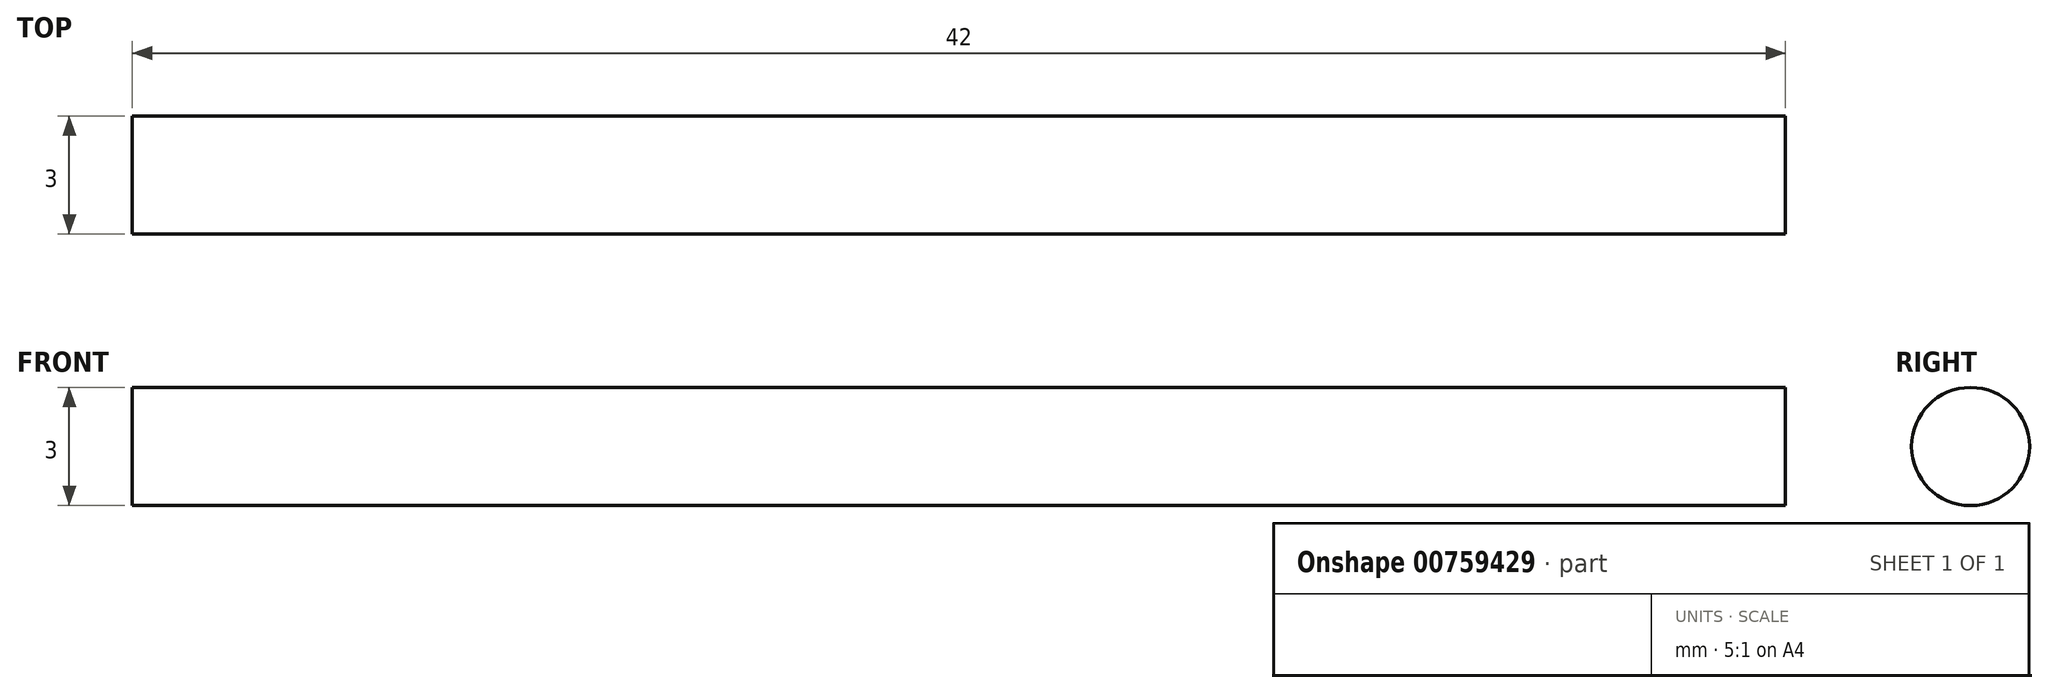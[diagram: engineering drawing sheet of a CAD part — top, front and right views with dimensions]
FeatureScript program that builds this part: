
annotation { "Feature Type Name" : "Feature", "Feature Type Description" : "" }
export const myFeature = defineFeature(function(context is Context, id is Id, definition is map)
    precondition{}
    {
        {
            var Q0;
            Q0=qCreatedBy(makeId("Right.planeOp"),FACE);
            var sketch = newSketch(context, id + "F0", { "sketchPlane" : qUnion([Q0])});
            skCircle(sketch, "E0", {"center": v(0, 0) * mm, "radius": 1.5 * mm});
            skSolve(sketch);
        }
        {
            var Q0;
            Q0 = qSketchRegion(id + "F0", true);
            extrude(context, id + "F1", {"entities" : qUnion([Q0]), "endBound" : BoundingType.SYMMETRIC, "depth" : 42 * mm, "offsetDistance" : 25 * mm});
        }
    });
